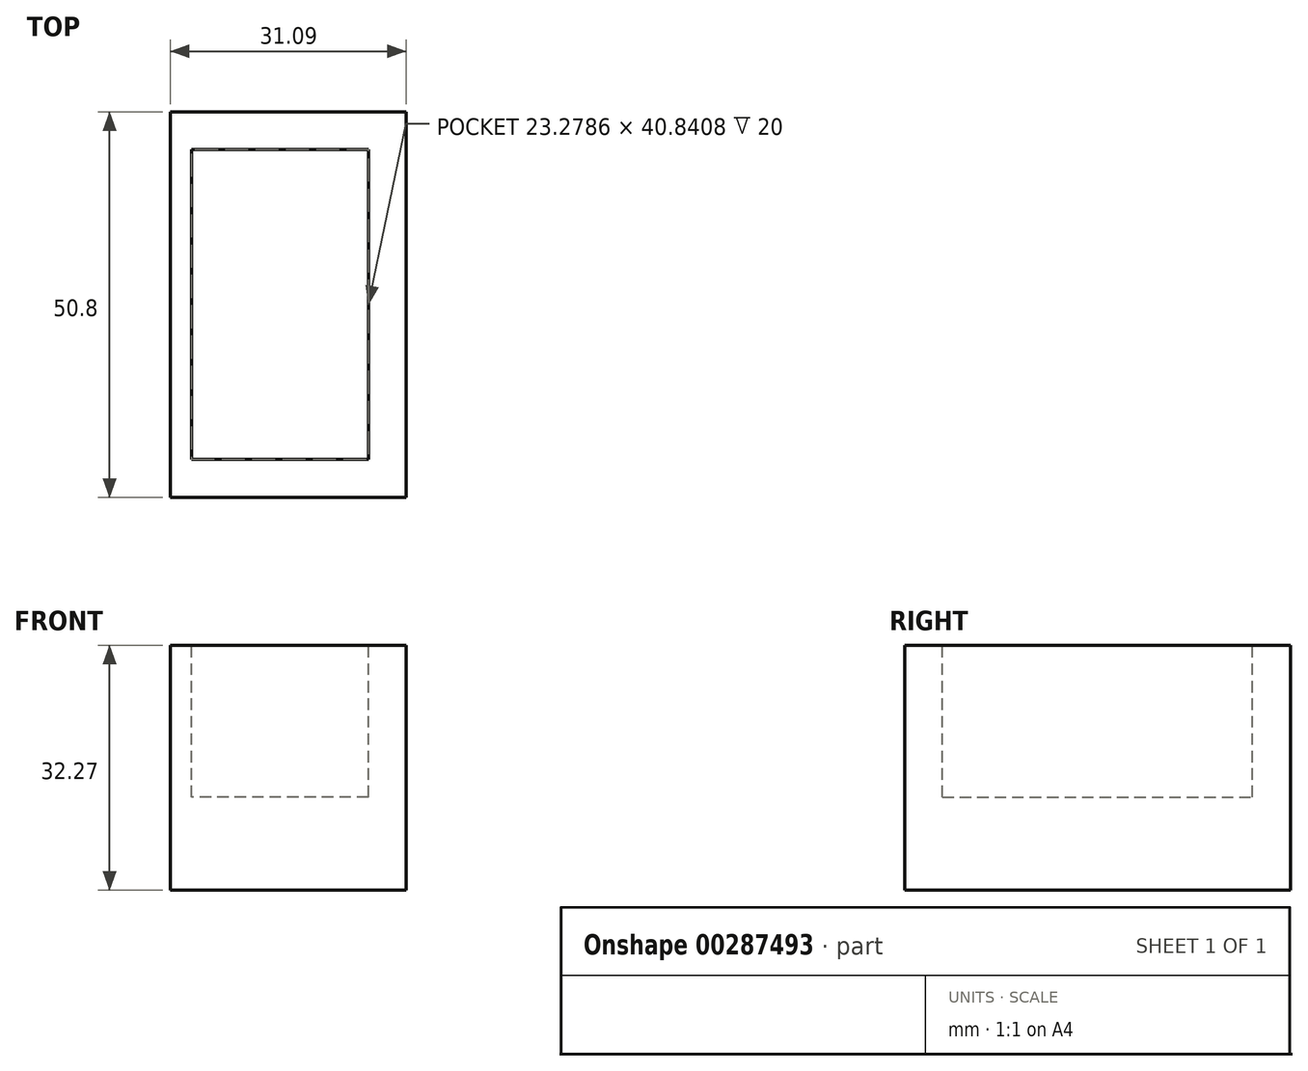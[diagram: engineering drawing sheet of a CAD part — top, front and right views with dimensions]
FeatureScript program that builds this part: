
annotation { "Feature Type Name" : "Feature", "Feature Type Description" : "" }
export const myFeature = defineFeature(function(context is Context, id is Id, definition is map)
    precondition{}
    {
        {
            var Q0;
            Q0=qCreatedBy(makeId("Front.planeOp"),FACE);
            var sketch = newSketch(context, id + "F0", { "sketchPlane" : qUnion([Q0])});
            skLineSegment(sketch, "E0", {"start": v(0, 31.23) * mm, "end": v(0, 0) * mm});
            skLineSegment(sketch, "E1", {"start": v(0, 0) * mm, "end": v(31.09, 0) * mm});
            skLineSegment(sketch, "E2", {"start": v(31.09, 0) * mm, "end": v(31.09, 32.27) * mm});
            skLineSegment(sketch, "E3", {"start": v(31.09, 32.27) * mm, "end": v(0, 32.27) * mm});
            skLineSegment(sketch, "E4", {"start": v(0, 32.27) * mm, "end": v(0, 24.6) * mm});
            skSolve(sketch);
        }
        {
            var Q0;
            Q0 = qSketchRegion(id + "F0", true);
            extrude(context, id + "F1", {"entities" : qUnion([Q0]), "depth" : 50.8 * mm});
        }
        {
            var Q0;
            Q0=makeQuery(id+"F1.opExtrude","SWEPT_FACE",FACE,{"disambiguationData":[OSD([sQuery(id+"F0.wireOp",EDGE,"E3")])]});
            var sketch = newSketch(context, id + "F2", { "sketchPlane" : qUnion([Q0])});
            skLineSegment(sketch, "E5.bottom", {"start": v(26.08, -45.82) * mm, "end": v(2.8, -45.82) * mm});
            skLineSegment(sketch, "E5.top", {"start": v(26.08, -4.98) * mm, "end": v(2.8, -4.98) * mm});
            skLineSegment(sketch, "E5.left", {"start": v(26.08, -45.82) * mm, "end": v(26.08, -4.98) * mm});
            skLineSegment(sketch, "E5.right", {"start": v(2.8, -45.82) * mm, "end": v(2.8, -4.98) * mm});
            skPoint(sketch, "E5.middle", {"position": v(14.44, -25.4) * mm});
            skPoint(sketch, "E5.middle.positionSnap0", {"position": v(31.09, -25.4) * mm});
            skPoint(sketch, "E5.centerSnap0", {"position": v(31.09, -25.4) * mm});
            skSolve(sketch);
        }
        {
            var Q0;
            Q0 = qSketchRegion(id + "F2", true);
            extrude(context, id + "F3", {"entities" : qUnion([Q0]), "operationType" : NewBodyOperationType.REMOVE, "oppositeDirection" : true, "depth" : 20 * mm});
        }
    });
